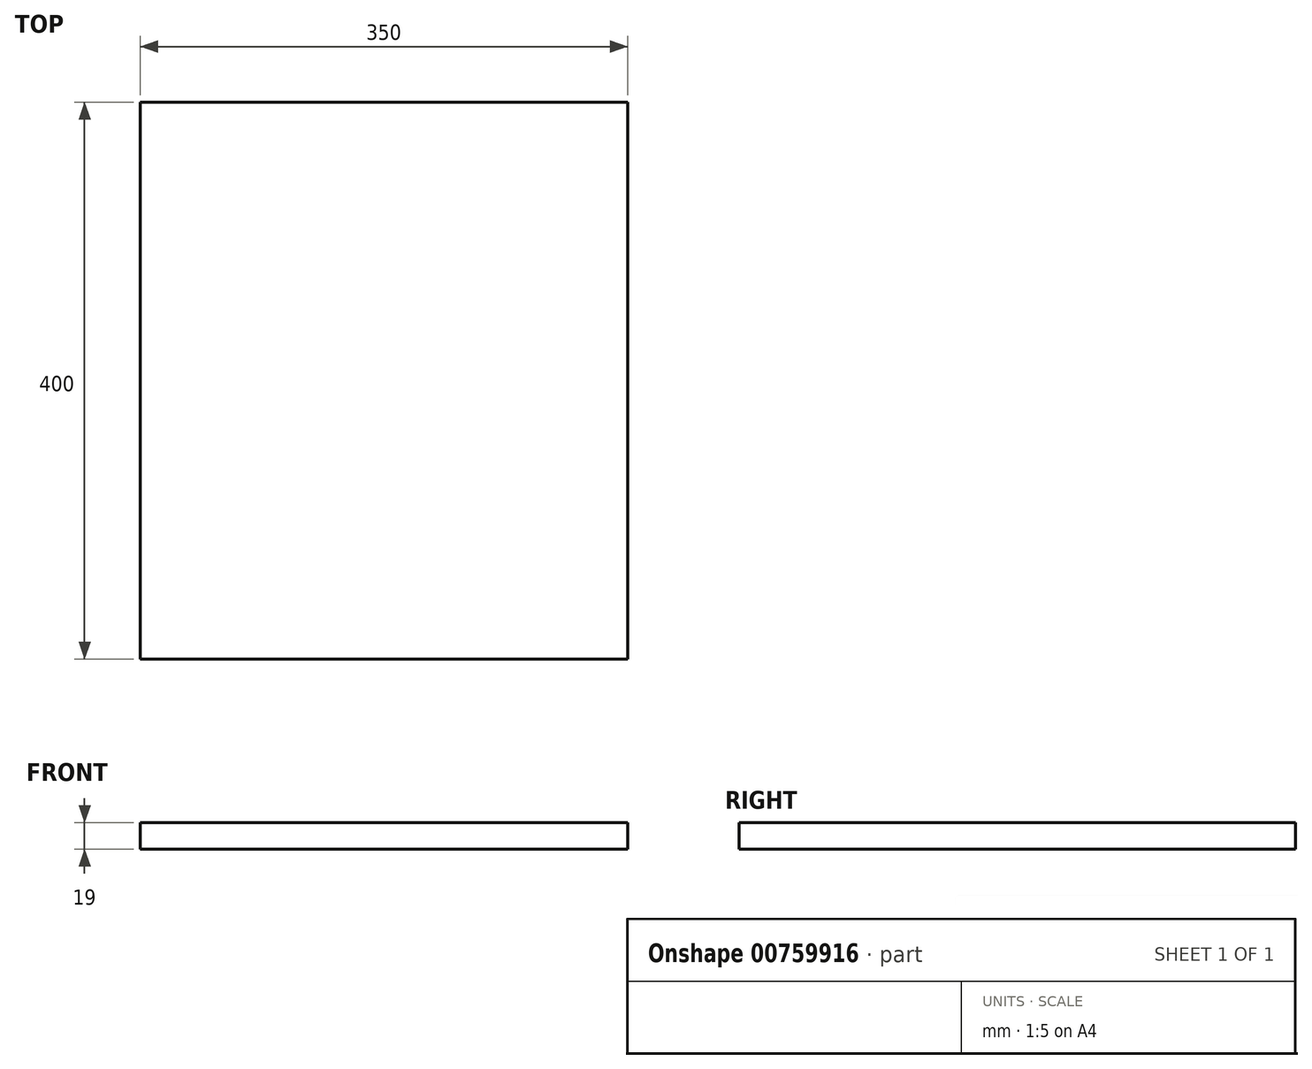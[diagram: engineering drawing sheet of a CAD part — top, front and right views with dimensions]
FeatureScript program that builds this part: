
annotation { "Feature Type Name" : "Feature", "Feature Type Description" : "" }
export const myFeature = defineFeature(function(context is Context, id is Id, definition is map)
    precondition{}
    {
        {
            var Q0;
            Q0=qCreatedBy(makeId("Top.planeOp"),FACE);
            var sketch = newSketch(context, id + "F0", { "sketchPlane" : qUnion([Q0])});
            skLineSegment(sketch, "E0.bottom", {"start": v(175, -200) * mm, "end": v(-175, -200) * mm});
            skLineSegment(sketch, "E0.top", {"start": v(175, 200) * mm, "end": v(-175, 200) * mm});
            skLineSegment(sketch, "E0.left", {"start": v(175, -200) * mm, "end": v(175, 200) * mm});
            skLineSegment(sketch, "E0.right", {"start": v(-175, -200) * mm, "end": v(-175, 200) * mm});
            skPoint(sketch, "E0.middle", {"position": v(0, 0) * mm});
            skSolve(sketch);
        }
        {
            var Q0;
            Q0 = qSketchRegion(id + "F0", true);
            extrude(context, id + "F1", {"entities" : qUnion([Q0]), "depth" : 19 * mm, "offsetDistance" : 25 * mm});
        }
    });
